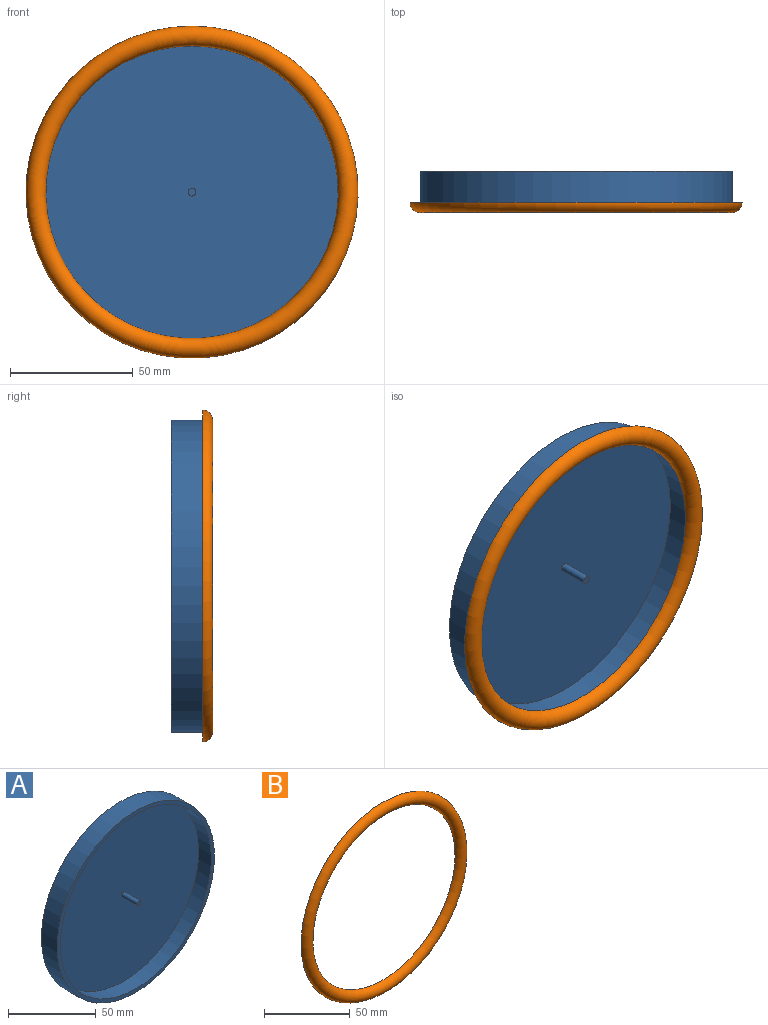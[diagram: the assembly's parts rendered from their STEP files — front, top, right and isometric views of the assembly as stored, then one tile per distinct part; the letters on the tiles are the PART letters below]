
ASSEMBLY  parts=2 mates=1
PART A: 7 faces, bbox 127x15.2x127 mm
  f0: cylinder r=63.5mm len=127mm, axis (0,1,0), area 5067.1mm2, adj f1,f2
  f1: plane 127x127mm, normal (0,-1,0), area 993.1mm2, adj f0,f3
  f2: plane 127x127mm, normal (0,1,0), area 12667.7mm2, adj f0
  f3: cylinder r=60.96mm len=121.92mm, axis (0,1,0), area 3891.5mm2, adj f1,f4
  f4: plane 121.92x121.92mm, normal (0,-1,0), area 11666.6mm2, adj f3,f5
  f5: cylinder r=1.59mm len=12.7mm, axis (0,1,0), area 126.7mm2, adj f4,f6
  f6: plane 3.18x3.18mm, normal (0,-1,0), area 7.9mm2, adj f5
PART B: 2 faces, bbox 146.2x6.9x146.2 mm
  f0: plane 135.09x135.09mm, normal (0,1,0), area 3226mm2, adj f1
  f1: torus R=63.5mm, axis (0,1,0), area 5067.4mm2, adj f0
PLACE A t=(29.81,37.28,8.02)mm
PLACE B t=(29.81,24.58,8.02)mm
MATE fastened A.f0 <-> B.f1  axis (0,-1,0) through (29.81,24.58,8.02)mm
